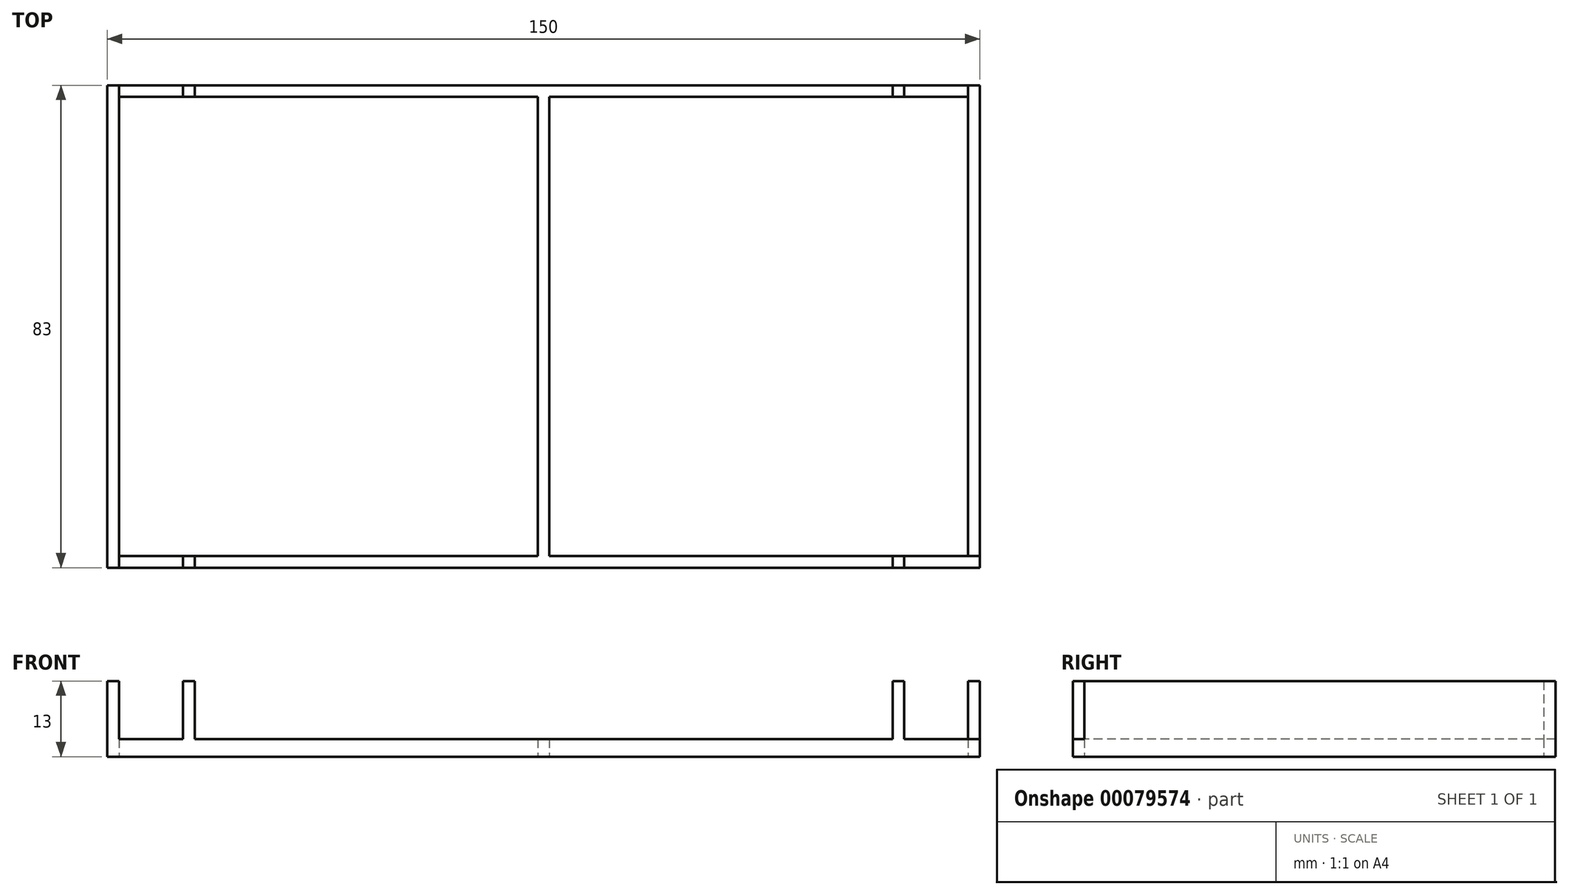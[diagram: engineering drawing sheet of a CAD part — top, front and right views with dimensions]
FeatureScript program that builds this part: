
annotation { "Feature Type Name" : "Feature", "Feature Type Description" : "" }
export const myFeature = defineFeature(function(context is Context, id is Id, definition is map)
    precondition{}
    {
        {
            var Q0;
            Q0=qCreatedBy(makeId("Top.planeOp"),FACE);
            var sketch = newSketch(context, id + "F0", { "sketchPlane" : qUnion([Q0])});
            skLineSegment(sketch, "E0.bottom", {"start": v(-75, -39.5) * mm, "end": v(75, -39.5) * mm});
            skLineSegment(sketch, "E0.top", {"start": v(-75, 39.5) * mm, "end": v(75, 39.5) * mm});
            skLineSegment(sketch, "E0.left", {"start": v(-75, -39.5) * mm, "end": v(-75, 39.5) * mm});
            skLineSegment(sketch, "E0.right", {"start": v(75, -39.5) * mm, "end": v(75, 39.5) * mm});
            skPoint(sketch, "E0.middle", {"position": v(0, 0) * mm});
            skLineSegment(sketch, "E1.bottom", {"start": v(-73, -41.5) * mm, "end": v(73, -41.5) * mm});
            skLineSegment(sketch, "E1.top", {"start": v(-73, 41.5) * mm, "end": v(73, 41.5) * mm});
            skLineSegment(sketch, "E1.left", {"start": v(-73, -41.5) * mm, "end": v(-73, 41.5) * mm});
            skLineSegment(sketch, "E1.right", {"start": v(73, -41.5) * mm, "end": v(73, 41.5) * mm});
            skLineSegment(sketch, "E2.bottom", {"start": v(-73, 41.5) * mm, "end": v(-75, 41.5) * mm});
            skLineSegment(sketch, "E2.top", {"start": v(-73, 39.5) * mm, "end": v(-75, 39.5) * mm});
            skLineSegment(sketch, "E2.left", {"start": v(-73, 39.5) * mm, "end": v(-73, 41.5) * mm});
            skLineSegment(sketch, "E2.right", {"start": v(-75, 39.5) * mm, "end": v(-75, 41.5) * mm});
            skLineSegment(sketch, "E3.bottom", {"start": v(73, 41.5) * mm, "end": v(75, 41.5) * mm});
            skLineSegment(sketch, "E3.top", {"start": v(73, 39.5) * mm, "end": v(75, 39.5) * mm});
            skLineSegment(sketch, "E3.left", {"start": v(73, 39.5) * mm, "end": v(73, 41.5) * mm});
            skLineSegment(sketch, "E3.right", {"start": v(75, 39.5) * mm, "end": v(75, 41.5) * mm});
            skLineSegment(sketch, "E4.bottom", {"start": v(75, -39.5) * mm, "end": v(73, -39.5) * mm});
            skLineSegment(sketch, "E4.top", {"start": v(75, -41.5) * mm, "end": v(73, -41.5) * mm});
            skLineSegment(sketch, "E4.left", {"start": v(75, -41.5) * mm, "end": v(75, -39.5) * mm});
            skLineSegment(sketch, "E4.right", {"start": v(73, -41.5) * mm, "end": v(73, -39.5) * mm});
            skLineSegment(sketch, "E5.bottom", {"start": v(-73, -41.5) * mm, "end": v(-75, -41.5) * mm});
            skLineSegment(sketch, "E5.top", {"start": v(-73, -39.5) * mm, "end": v(-75, -39.5) * mm});
            skLineSegment(sketch, "E5.left", {"start": v(-73, -39.5) * mm, "end": v(-73, -41.5) * mm});
            skLineSegment(sketch, "E5.right", {"start": v(-75, -39.5) * mm, "end": v(-75, -41.5) * mm});
            skLineSegment(sketch, "E6.bottom", {"start": v(-1, 41.5) * mm, "end": v(1, 41.5) * mm});
            skLineSegment(sketch, "E6.top", {"start": v(-1, -41.5) * mm, "end": v(1, -41.5) * mm});
            skLineSegment(sketch, "E6.left", {"start": v(-1, 41.5) * mm, "end": v(-1, -41.5) * mm});
            skLineSegment(sketch, "E6.right", {"start": v(1, 41.5) * mm, "end": v(1, -41.5) * mm});
            skLineSegment(sketch, "E7.bottom", {"start": v(-62, -41.5) * mm, "end": v(62, -41.5) * mm});
            skLineSegment(sketch, "E7.top", {"start": v(-62, 41.5) * mm, "end": v(62, 41.5) * mm});
            skLineSegment(sketch, "E7.left", {"start": v(-62, -41.5) * mm, "end": v(-62, 41.5) * mm});
            skLineSegment(sketch, "E7.right", {"start": v(62, -41.5) * mm, "end": v(62, 41.5) * mm});
            skLineSegment(sketch, "E8.bottom", {"start": v(-60, -41.5) * mm, "end": v(60, -41.5) * mm});
            skLineSegment(sketch, "E8.top", {"start": v(-60, 41.5) * mm, "end": v(60, 41.5) * mm});
            skLineSegment(sketch, "E8.left", {"start": v(-60, -41.5) * mm, "end": v(-60, 41.5) * mm});
            skLineSegment(sketch, "E8.right", {"start": v(60, -41.5) * mm, "end": v(60, 41.5) * mm});
            skSolve(sketch);
        }
        {
            var Q0;
            Q0 = qSketchRegion(id + "F0", true);
            var Q1;
            {var subQ0=sQuery(id+"F0.wireOp",EDGE,"E6.left");var subQ1=sQuery(id+"F0.wireOp",EDGE,"E0.bottom");var subQ2=makeQuery(id+"F0.imprint","INTERSECT",VERTEX,{"derivedFrom":[subQ1,subQ0]});Q1=makeQuery(id+"F0.imprint","IMPRINT",FACE,{"disambiguationData":[TD([[makeQuery(id+"F0.imprint","IMPRINT",EDGE,{"disambiguationData":[TD([[subQ2,-1.0]])],"derivedFrom":subQ1}),1.0]])]});}
            extrude(context, id + "F1", {"entities" : qUnion([Q0, Q1]), "depth" : 3 * mm});
        }
        {
            var Q0;
            {var subQ0=sQuery(id+"F0.wireOp",EDGE,"E7.left");var subQ1=sQuery(id+"F0.wireOp",EDGE,"E0.bottom");var subQ2=makeQuery(id+"F0.imprint","INTERSECT",VERTEX,{"derivedFrom":[subQ1,subQ0]});Q0=makeQuery(id+"F0.imprint","IMPRINT",FACE,{"disambiguationData":[TD([[makeQuery(id+"F0.imprint","IMPRINT",EDGE,{"disambiguationData":[TD([[subQ2,-1.0]])],"derivedFrom":subQ1}),-1.0]])]});}
            var Q1;
            {var subQ0=sQuery(id+"F0.wireOp",EDGE,"E7.left");var subQ1=sQuery(id+"F0.wireOp",EDGE,"E0.top");var subQ2=makeQuery(id+"F0.imprint","INTERSECT",VERTEX,{"derivedFrom":[subQ1,subQ0]});Q1=makeQuery(id+"F0.imprint","IMPRINT",FACE,{"disambiguationData":[TD([[makeQuery(id+"F0.imprint","IMPRINT",EDGE,{"disambiguationData":[TD([[subQ2,-1.0]])],"derivedFrom":subQ1}),1.0]])]});}
            var Q2;
            Q2=makeQuery(id+"F0.imprint","IMPRINT",FACE,{"disambiguationData":[TD([[makeQuery(id+"F0.imprint","IMPRINT",EDGE,{"derivedFrom":sQuery(id+"F0.wireOp",EDGE,"E0.left")}),-1.0]])]});
            var Q3;
            Q3=makeQuery(id+"F0.imprint","IMPRINT",FACE,{"disambiguationData":[TD([[makeQuery(id+"F0.imprint","IMPRINT",EDGE,{"derivedFrom":sQuery(id+"F0.wireOp",EDGE,"E5.bottom")}),-1.0]])]});
            var Q4;
            {var subQ0=sQuery(id+"F0.wireOp",EDGE,"E5.left");Q4=makeQuery(id+"F0.imprint","IMPRINT",FACE,{"disambiguationData":[TD([[makeQuery(id+"F0.imprint","IMPRINT",EDGE,{"derivedFrom":subQ0}),1.0]])]});}
            var Q5;
            {var subQ0=sQuery(id+"F0.wireOp",EDGE,"E2.left");Q5=makeQuery(id+"F0.imprint","IMPRINT",FACE,{"disambiguationData":[TD([[makeQuery(id+"F0.imprint","IMPRINT",EDGE,{"derivedFrom":subQ0}),-1.0]])]});}
            var Q6;
            Q6=makeQuery(id+"F0.imprint","IMPRINT",FACE,{"disambiguationData":[TD([[makeQuery(id+"F0.imprint","IMPRINT",EDGE,{"derivedFrom":sQuery(id+"F0.wireOp",EDGE,"E2.bottom")}),1.0]])]});
            var Q7;
            {var subQ0=sQuery(id+"F0.wireOp",EDGE,"E8.right");var subQ1=sQuery(id+"F0.wireOp",EDGE,"E0.top");var subQ2=makeQuery(id+"F0.imprint","INTERSECT",VERTEX,{"derivedFrom":[subQ1,subQ0]});Q7=makeQuery(id+"F0.imprint","IMPRINT",FACE,{"disambiguationData":[TD([[makeQuery(id+"F0.imprint","IMPRINT",EDGE,{"disambiguationData":[TD([[subQ2,-1.0]])],"derivedFrom":subQ1}),1.0]])]});}
            var Q8;
            {var subQ0=sQuery(id+"F0.wireOp",EDGE,"E3.left");Q8=makeQuery(id+"F0.imprint","IMPRINT",FACE,{"disambiguationData":[TD([[makeQuery(id+"F0.imprint","IMPRINT",EDGE,{"derivedFrom":subQ0}),1.0]])]});}
            var Q9;
            Q9=makeQuery(id+"F0.imprint","IMPRINT",FACE,{"disambiguationData":[TD([[makeQuery(id+"F0.imprint","IMPRINT",EDGE,{"derivedFrom":sQuery(id+"F0.wireOp",EDGE,"E3.bottom")}),-1.0]])]});
            var Q10;
            Q10=makeQuery(id+"F0.imprint","IMPRINT",FACE,{"disambiguationData":[TD([[makeQuery(id+"F0.imprint","IMPRINT",EDGE,{"derivedFrom":sQuery(id+"F0.wireOp",EDGE,"E0.right")}),1.0]])]});
            var Q11;
            Q11=makeQuery(id+"F0.imprint","IMPRINT",FACE,{"disambiguationData":[TD([[makeQuery(id+"F0.imprint","IMPRINT",EDGE,{"derivedFrom":sQuery(id+"F0.wireOp",EDGE,"E4.bottom")}),1.0]])]});
            var Q12;
            {var subQ0=sQuery(id+"F0.wireOp",EDGE,"E4.right");Q12=makeQuery(id+"F0.imprint","IMPRINT",FACE,{"disambiguationData":[TD([[makeQuery(id+"F0.imprint","IMPRINT",EDGE,{"derivedFrom":subQ0}),1.0]])]});}
            var Q13;
            {var subQ0=sQuery(id+"F0.wireOp",EDGE,"E8.right");var subQ1=sQuery(id+"F0.wireOp",EDGE,"E0.bottom");var subQ2=makeQuery(id+"F0.imprint","INTERSECT",VERTEX,{"derivedFrom":[subQ1,subQ0]});Q13=makeQuery(id+"F0.imprint","IMPRINT",FACE,{"disambiguationData":[TD([[makeQuery(id+"F0.imprint","IMPRINT",EDGE,{"disambiguationData":[TD([[subQ2,-1.0]])],"derivedFrom":subQ1}),-1.0]])]});}
            extrude(context, id + "F2", {"entities" : qUnion([Q0, Q1, Q2, Q3, Q4, Q5, Q6, Q7, Q8, Q9, Q10, Q11, Q12, Q13]), "operationType" : NewBodyOperationType.ADD, "depth" : 13 * mm});
        }
    });
